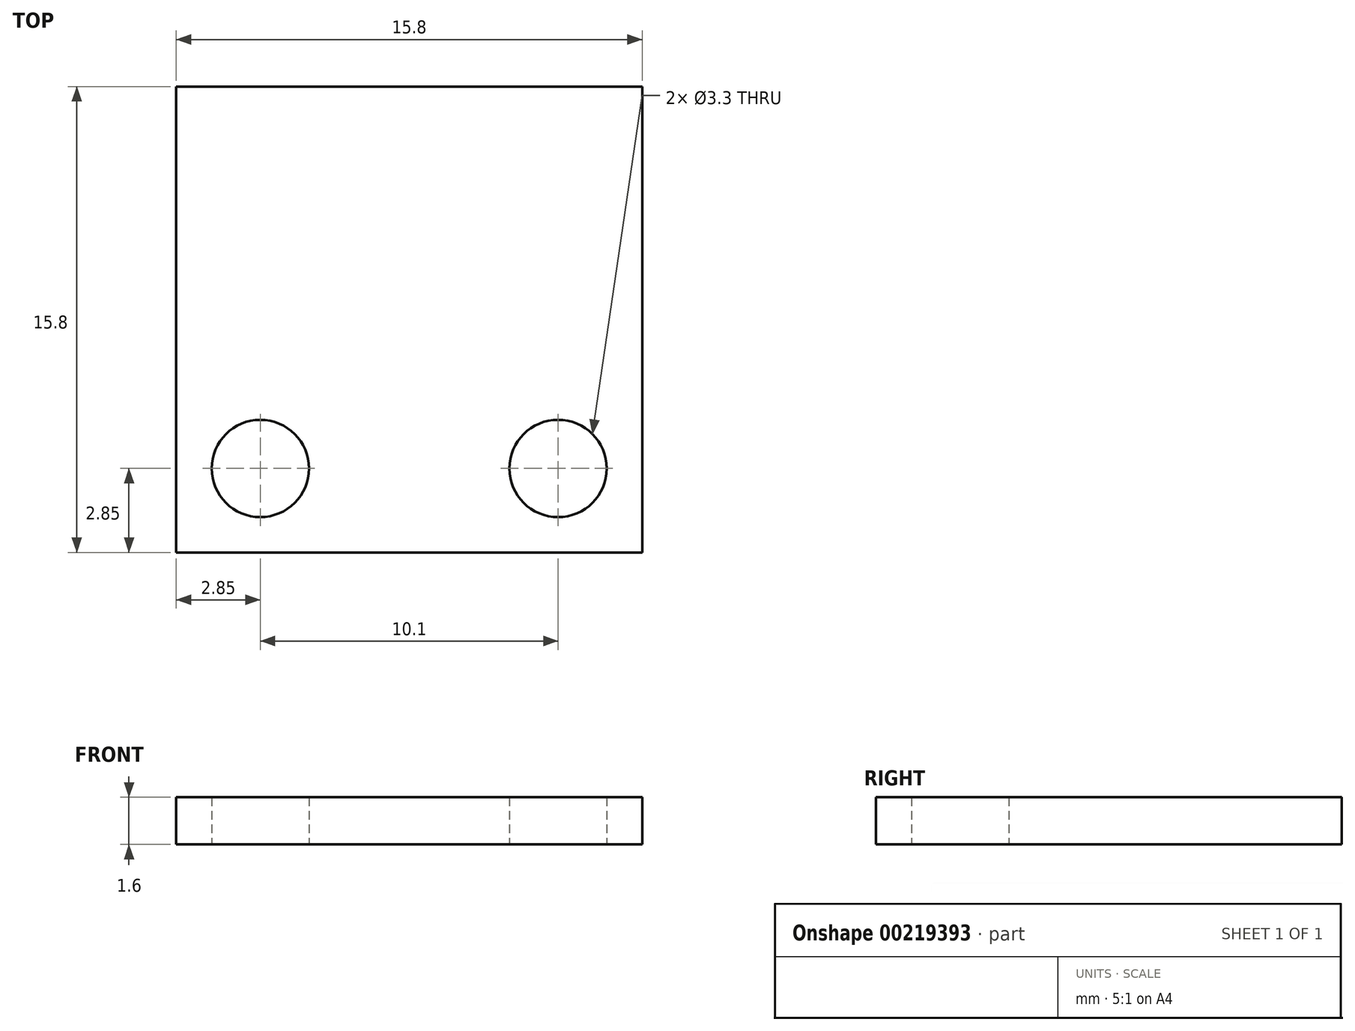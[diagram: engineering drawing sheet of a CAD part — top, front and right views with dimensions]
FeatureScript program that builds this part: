
annotation { "Feature Type Name" : "Feature", "Feature Type Description" : "" }
export const myFeature = defineFeature(function(context is Context, id is Id, definition is map)
    precondition{}
    {
        {
            var Q0;
            Q0=qCreatedBy(makeId("Top.planeOp"),FACE);
            var sketch = newSketch(context, id + "F0", { "sketchPlane" : qUnion([Q0])});
            skLineSegment(sketch, "E0.bottom", {"start": v(7.9, 7.9) * mm, "end": v(-7.9, 7.9) * mm});
            skLineSegment(sketch, "E0.top", {"start": v(7.9, -7.9) * mm, "end": v(-7.9, -7.9) * mm});
            skLineSegment(sketch, "E0.left", {"start": v(7.9, 7.9) * mm, "end": v(7.9, -7.9) * mm});
            skLineSegment(sketch, "E0.right", {"start": v(-7.9, 7.9) * mm, "end": v(-7.9, -7.9) * mm});
            skPoint(sketch, "E0.middle", {"position": v(0, 0) * mm});
            skCircle(sketch, "E1", {"center": v(-5.05, -5.05) * mm, "radius": 1.65 * mm});
            skCircle(sketch, "E2", {"center": v(5.05, -5.05) * mm, "radius": 1.65 * mm});
            skSolve(sketch);
        }
        {
            var Q0;
            Q0=makeQuery(id+"F0.imprint","IMPRINT",FACE,{"disambiguationData":[TD([[makeQuery(id+"F0.imprint","IMPRINT",EDGE,{"derivedFrom":sQuery(id+"F0.wireOp",EDGE,"E0.bottom")}),1.0]])]});
            extrude(context, id + "F1", {"entities" : qUnion([Q0]), "depth" : 1.6 * mm});
        }
    });
